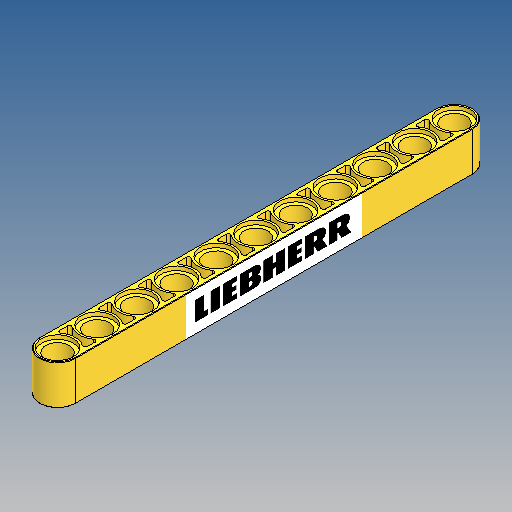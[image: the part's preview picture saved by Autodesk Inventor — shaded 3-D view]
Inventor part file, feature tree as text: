
AUTODESK INVENTOR PART (.ipt)
format: ipt  version: 2025 (Build 290162010, 162A)  size: 474,624 bytes
history: native  units: mm
features: sketch x4, extrude x3, other x2, mirror x1, fillet x1
ambient origin geometry x8: Origin, YZ Plane, XZ Plane, XY Plane, X Axis, Y Axis, Z Axis, Center Point
bodies: Solid1 (feature_tree)
feature tree (11):
  extrude  "Extrusion1"  Depth=7.2mm
  sketch  "Sketch6"  dims[d48=80.0mm d49=6.4mm d50=4.8mm]
  extrude  "Extrusion7"  Depth=3.1mm TaperAngle=0.0deg
  extrude  "Extrusion8"  Depth=6.4mm
  mirror  "Mirror1"
  fillet  "Fillet2"  Radius=4.8mm
  other  "Aufkleber1"
  sketch  "Sketch1"  dims[d14=8.0mm d15=0.0mm d32=7.2mm]
  sketch  "Skizze - Rechteckige Anordnung1"  dims[d41=0.8mm d42=0.0mm d43=3.1mm d44=0.0mm]
  sketch  "Skizze7"  dims[d51=8.0mm d52=0.8mm d53=100.0mm d55=8.0mm d56=10.0mm d58=10.0mm d60=0.4mm d61=0.1mm]
  other  "Bild2"
